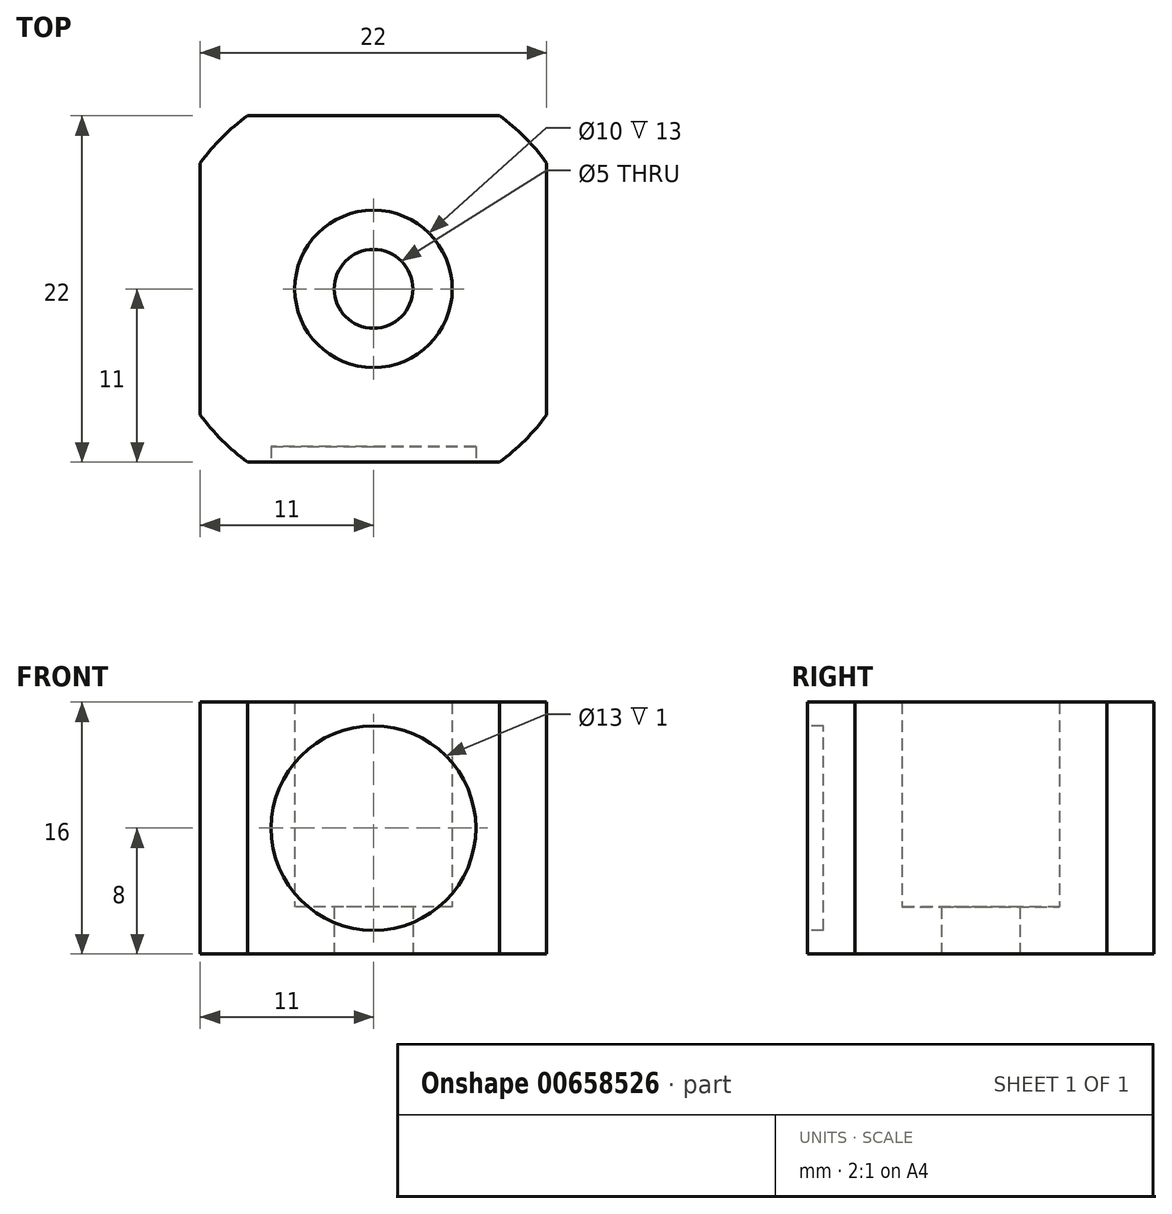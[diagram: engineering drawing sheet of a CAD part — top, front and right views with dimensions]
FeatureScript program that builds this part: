
annotation { "Feature Type Name" : "Feature", "Feature Type Description" : "" }
export const myFeature = defineFeature(function(context is Context, id is Id, definition is map)
    precondition{}
    {
        {
            var Q0;
            Q0=qCreatedBy(makeId("Top.planeOp"),FACE);
            var sketch = newSketch(context, id + "F0", { "sketchPlane" : qUnion([Q0])});
            skCircle(sketch, "E0", {"center": v(0, 0) * mm, "radius": 5 * mm});
            skCircle(sketch, "E1", {"center": v(0, 0) * mm, "radius": 13.6 * mm});
            skLineSegment(sketch, "E2.bottom", {"start": v(11, 11) * mm, "end": v(-11, 11) * mm});
            skLineSegment(sketch, "E2.top", {"start": v(11, -11) * mm, "end": v(-11, -11) * mm});
            skLineSegment(sketch, "E2.left", {"start": v(11, 11) * mm, "end": v(11, -11) * mm});
            skLineSegment(sketch, "E2.right", {"start": v(-11, 11) * mm, "end": v(-11, -11) * mm});
            skCircle(sketch, "E3", {"center": v(0, 0) * mm, "radius": 11 * mm, "construction": true});
            skPoint(sketch, "E4", {"position": v(-8, -11) * mm});
            skPoint(sketch, "E5", {"position": v(8, -11) * mm});
            skPoint(sketch, "E6", {"position": v(0, 13.6) * mm});
            skPoint(sketch, "E7", {"position": v(0, 5) * mm});
            skCircle(sketch, "E8", {"center": v(0, 0) * mm, "radius": 2.5 * mm});
            skSolve(sketch);
        }
        {
            var Q0;
            Q0=qCreatedBy(makeId("Front.planeOp"),FACE);
            var sketch = newSketch(context, id + "F1", { "sketchPlane" : qUnion([Q0])});
            skLineSegment(sketch, "E9", {"start": v(0, 0) * mm, "end": v(0, 33.4) * mm, "construction": true});
            skSolve(sketch);
        }
        {
            var Q0;
            Q0=makeQuery(id+"F0.imprint","IMPRINT",FACE,{"disambiguationData":[TD([[makeQuery(id+"F0.imprint","IMPRINT",EDGE,{"derivedFrom":sQuery(id+"F0.wireOp",EDGE,"E0")}),-1.0]])]});
            extrude(context, id + "F2", {"entities" : qUnion([Q0]), "depth" : 16 * mm, "offsetDistance" : 25 * mm});
        }
        {
            var Q0;
            Q0=makeQuery(id+"F2.opExtrude","SWEPT_FACE",FACE,{"disambiguationData":[OSD([sQuery(id+"F0.wireOp",EDGE,"E2.top")])]});
            var sketch = newSketch(context, id + "F3", { "sketchPlane" : qUnion([Q0])});
            skLineSegment(sketch, "E10.0.0", {"start": v(-8, 0) * mm, "end": v(8, 0) * mm});
            skLineSegment(sketch, "E10.0.1", {"start": v(-8, 16) * mm, "end": v(-8, 0) * mm});
            skLineSegment(sketch, "E10.0.2", {"start": v(8, 16) * mm, "end": v(-8, 16) * mm});
            skLineSegment(sketch, "E10.0.3", {"start": v(8, 0) * mm, "end": v(8, 16) * mm});
            skCircle(sketch, "E11", {"center": v(0, 8) * mm, "radius": 6.5 * mm});
            skSolve(sketch);
        }
        {
            var Q0;
            Q0=makeQuery(id+"F3.imprint","IMPRINT",FACE,{"disambiguationData":[TD([[makeQuery(id+"F3.imprint","IMPRINT",EDGE,{"derivedFrom":sQuery(id+"F3.wireOp",EDGE,"E11")}),1.0]])]});
            extrude(context, id + "F4", {"entities" : qUnion([Q0]), "operationType" : NewBodyOperationType.REMOVE, "oppositeDirection" : true, "depth" : 1 * mm, "offsetDistance" : 25 * mm});
        }
        {
            var Q0;
            Q0=makeQuery(id+"F0.imprint","IMPRINT",FACE,{"disambiguationData":[TD([[makeQuery(id+"F0.imprint","IMPRINT",EDGE,{"derivedFrom":sQuery(id+"F0.wireOp",EDGE,"E0")}),1.0]])]});
            extrude(context, id + "F5", {"entities" : qUnion([Q0]), "operationType" : NewBodyOperationType.ADD, "depth" : 3 * mm, "offsetDistance" : 25 * mm});
        }
    });
